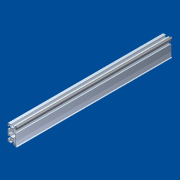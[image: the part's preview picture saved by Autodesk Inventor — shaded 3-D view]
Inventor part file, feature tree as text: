
AUTODESK INVENTOR PART (.ipt)
format: ipt  version: 2012 SP1 (Build 160190100, 190)  size: 405,504 bytes
history: native  units: in
note: dims shown in document units (in); Inventor stores cm internally (conversion verified against a paired STEP export)
features: other x1, imported_body x1, extrude x1, sketch x1
ambient origin geometry x8: Origin, YZ Plane, XZ Plane, XY Plane, X Axis, Y Axis, Z Axis, Center Point
feature tree (4):
  other  "MAKER_SLIDE_6_100"
  imported_body  "Base1"
  extrude  "Extrusion1"  [1 undecoded]
  sketch  "Sketch1"  dims[d0=10.8268in d1=0.0in]
note: 1 required parameter value undecoded (feature->parameter linkage not recoverable at this tier; creation-order binding heuristic only, values carry confidence <= 0.55)
